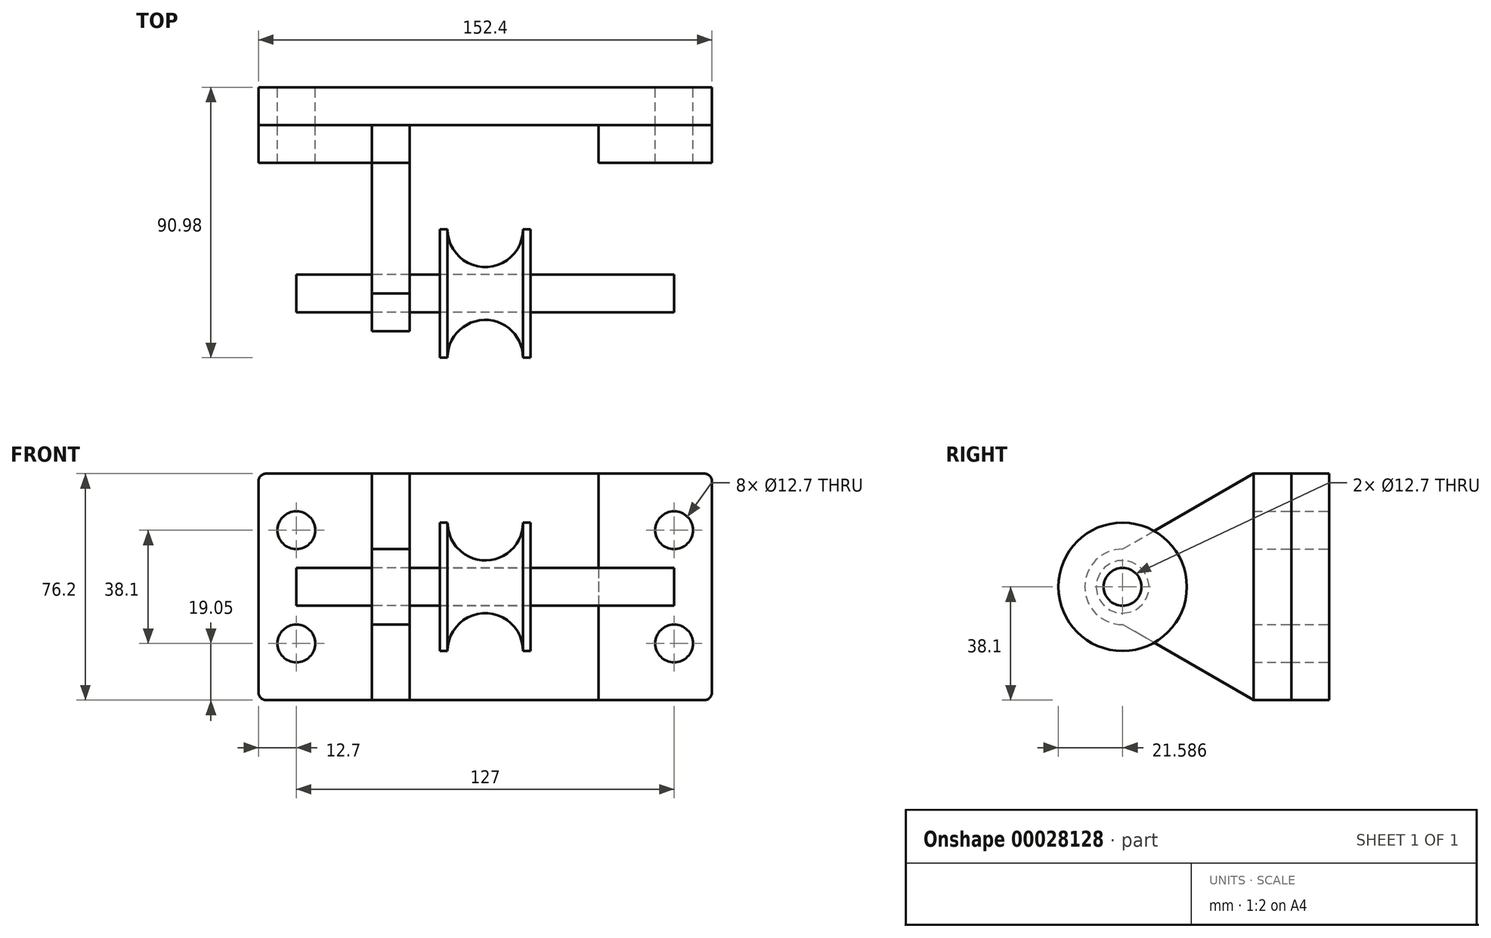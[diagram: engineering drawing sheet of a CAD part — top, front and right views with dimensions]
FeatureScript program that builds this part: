
annotation { "Feature Type Name" : "Feature", "Feature Type Description" : "" }
export const myFeature = defineFeature(function(context is Context, id is Id, definition is map)
    precondition{}
    {
        {
            var Q0;
            Q0=qCreatedBy(makeId("Front.planeOp"),FACE);
            var sketch = newSketch(context, id + "F0", { "sketchPlane" : qUnion([Q0])});
            skLineSegment(sketch, "E0.bottom", {"start": v(-76.2, 38.1) * mm, "end": v(76.2, 38.1) * mm});
            skLineSegment(sketch, "E0.top", {"start": v(-76.2, -38.1) * mm, "end": v(76.2, -38.1) * mm});
            skLineSegment(sketch, "E0.left", {"start": v(-76.2, 38.1) * mm, "end": v(-76.2, -38.1) * mm});
            skLineSegment(sketch, "E0.right", {"start": v(76.2, 38.1) * mm, "end": v(76.2, -38.1) * mm});
            skLineSegment(sketch, "E1", {"start": v(0, 38.1) * mm, "end": v(0, -38.1) * mm, "construction": true});
            skLineSegment(sketch, "E2", {"start": v(-76.2, 0) * mm, "end": v(76.2, 0) * mm, "construction": true});
            skCircle(sketch, "E3", {"center": v(-63.5, 19.05) * mm, "radius": 6.35 * mm});
            skCircle(sketch, "E4.MirrorC", {"center": v(63.5, 19.05) * mm, "radius": 6.35 * mm});
            skCircle(sketch, "E5.MirrorC", {"center": v(-63.5, -19.05) * mm, "radius": 6.35 * mm});
            skCircle(sketch, "E6.MirrorC", {"center": v(63.5, -19.05) * mm, "radius": 6.35 * mm});
            skSolve(sketch);
        }
        {
            var Q0;
            Q0=makeQuery(id+"F0.imprint","IMPRINT",FACE,{"disambiguationData":[TD([[makeQuery(id+"F0.imprint","IMPRINT",EDGE,{"derivedFrom":sQuery(id+"F0.wireOp",EDGE,"E0.bottom")}),-1.0]])]});
            extrude(context, id + "F1", {"entities" : qUnion([Q0]), "depth" : 12.7 * mm});
        }
        {
            var Q0;
            Q0=makeQuery(id+"F1.opExtrude","SWEPT_EDGE",EDGE,{"disambiguationData":[OSD([sQuery(id+"F0.wireOp",EDGE,"E0.bottom"),sQuery(id+"F0.wireOp",EDGE,"E0.left")])]});
            var Q1;
            Q1=makeQuery(id+"F1.opExtrude","SWEPT_EDGE",EDGE,{"disambiguationData":[OSD([sQuery(id+"F0.wireOp",EDGE,"E0.top"),sQuery(id+"F0.wireOp",EDGE,"E0.left")])]});
            var Q2;
            Q2=makeQuery(id+"F1.opExtrude","SWEPT_EDGE",EDGE,{"disambiguationData":[OSD([sQuery(id+"F0.wireOp",EDGE,"E0.bottom"),sQuery(id+"F0.wireOp",EDGE,"E0.right")])]});
            var Q3;
            Q3=makeQuery(id+"F1.opExtrude","SWEPT_EDGE",EDGE,{"disambiguationData":[OSD([sQuery(id+"F0.wireOp",EDGE,"E0.top"),sQuery(id+"F0.wireOp",EDGE,"E0.right")])]});
            fillet(context, id + "F2", {"entities" : qUnion([Q0, Q1, Q2, Q3]), "radius" : 2.54 * mm, "tangentPropagation" : true, "allowEdgeOverflow" : false});
        }
        {
            var Q0;
            Q0=makeQuery(id+"F1.opExtrude","CAP_FACE",FACE,{"disambiguationData":[OSD([sQuery(id+"F0.wireOp",EDGE,"E0.bottom"),sQuery(id+"F0.wireOp",EDGE,"E0.top"),sQuery(id+"F0.wireOp",EDGE,"E0.left"),sQuery(id+"F0.wireOp",EDGE,"E0.right"),sQuery(id+"F0.wireOp",EDGE,"E3"),sQuery(id+"F0.wireOp",EDGE,"E4.MirrorC"),sQuery(id+"F0.wireOp",EDGE,"E5.MirrorC"),sQuery(id+"F0.wireOp",EDGE,"E6.MirrorC")])],"isStart":false});
            var sketch = newSketch(context, id + "F3", { "sketchPlane" : qUnion([Q0])});
            skLineSegment(sketch, "E7.bottom", {"start": v(-76.2, 38.1) * mm, "end": v(-38.1, 38.1) * mm});
            skLineSegment(sketch, "E7.top", {"start": v(-76.2, -38.1) * mm, "end": v(-38.1, -38.1) * mm});
            skLineSegment(sketch, "E7.left", {"start": v(-76.2, 38.1) * mm, "end": v(-76.2, -38.1) * mm});
            skLineSegment(sketch, "E7.right", {"start": v(-38.1, 38.1) * mm, "end": v(-38.1, -38.1) * mm});
            skSolve(sketch);
        }
        {
            var Q0;
            {var subQ8=sQuery(id+"F3.wireOp",EDGE,"E7.right");Q0=makeQuery(id+"F3.imprint","IMPRINT",FACE,{"disambiguationData":[TD([[makeQuery(id+"F3.imprint","IMPRINT",EDGE,{"derivedFrom":subQ8}),-1.0]])]});}
            extrude(context, id + "F4", {"entities" : qUnion([Q0]), "depth" : 12.7 * mm});
        }
        {
            var Q0;
            Q0=makeQuery(id+"F4.opExtrude","SWEPT_FACE",FACE,{"disambiguationData":[OSD([sQuery(id+"F3.wireOp",EDGE,"E7.right")])]});
            cPlane(context, id + "F5", {"entities" : qUnion([Q0]), "cplaneType" : CPlaneType.OFFSET, "offset" : 0 * mm, "width" : 152.4 * mm, "height" : 152.4 * mm});
        }
        {
            var Q0;
            Q0=qCreatedBy(id+"F5.planeOp",FACE);
            var sketch = newSketch(context, id + "F6", { "sketchPlane" : qUnion([Q0])});
            skLineSegment(sketch, "E8.0", {"start": v(-25.4, -38.1) * mm, "end": v(-12.7, -38.1) * mm});
            skLineSegment(sketch, "E9.0", {"start": v(-25.4, 38.1) * mm, "end": v(-12.7, 38.1) * mm});
            skLineSegment(sketch, "E10.0", {"start": v(-25.4, 38.1) * mm, "end": v(-25.4, -38.1) * mm});
            skLineSegment(sketch, "E11", {"start": v(-12.7, -38.1) * mm, "end": v(-12.7, 38.1) * mm});
            skLineSegment(sketch, "E12", {"start": v(-25.4, -38.1) * mm, "end": v(-69.4, -12.7) * mm});
            skLineSegment(sketch, "E13", {"start": v(-69.4, -12.7) * mm, "end": v(-69.4, 12.7) * mm});
            skLineSegment(sketch, "E14", {"start": v(-69.4, 12.7) * mm, "end": v(-25.4, 38.1) * mm});
            skCircle(sketch, "E15", {"center": v(-69.4, 0) * mm, "radius": 6.35 * mm});
            skCircle(sketch, "E16", {"center": v(-69.4, 0) * mm, "radius": 12.7 * mm});
            skSolve(sketch);
        }
        {
            var Q0;
            Q0=makeQuery(id+"F6.imprint","IMPRINT",FACE,{"disambiguationData":[TD([[makeQuery(id+"F6.imprint","IMPRINT",EDGE,{"derivedFrom":sQuery(id+"F6.wireOp",EDGE,"E8.0")}),1.0]])]});
            var Q1;
            Q1=makeQuery(id+"F6.imprint","IMPRINT",FACE,{"disambiguationData":[TD([[makeQuery(id+"F6.imprint","IMPRINT",EDGE,{"derivedFrom":sQuery(id+"F6.wireOp",EDGE,"E10.0")}),-1.0]])]});
            var Q2;
            {var subQ1=sQuery(id+"F6.wireOp",EDGE,"E13");var subQ4=sQuery(id+"F6.wireOp",EDGE,"E15");var subQ6=makeQuery(id+"F6.imprint","INTERSECT",VERTEX,{"disambiguationData":[OD(0.0)],"derivedFrom":[subQ1,subQ4]});Q2=makeQuery(id+"F6.imprint","IMPRINT",FACE,{"disambiguationData":[TD([[makeQuery(id+"F6.imprint","IMPRINT",EDGE,{"disambiguationData":[TD([[subQ6,1.0]])],"derivedFrom":subQ4}),-1.0]])]});}
            var Q3;
            {var subQ1=sQuery(id+"F6.wireOp",EDGE,"E13");var subQ4=sQuery(id+"F6.wireOp",EDGE,"E15");var subQ6=makeQuery(id+"F6.imprint","INTERSECT",VERTEX,{"disambiguationData":[OD(0.0)],"derivedFrom":[subQ1,subQ4]});Q3=makeQuery(id+"F6.imprint","IMPRINT",FACE,{"disambiguationData":[TD([[makeQuery(id+"F6.imprint","IMPRINT",EDGE,{"disambiguationData":[TD([[subQ6,-1.0]])],"derivedFrom":subQ4}),-1.0]])]});}
            extrude(context, id + "F7", {"entities" : qUnion([Q0, Q1, Q2, Q3]), "depth" : 12.7 * mm});
        }
        {
            var Q0;
            Q0=makeQuery(id+"F4.opExtrude","SWEPT_BODY",BODY,{"disambiguationData":[OSD([sQuery(id+"F0.wireOp",EDGE,"E0.bottom"),sQuery(id+"F0.wireOp",EDGE,"E0.top"),sQuery(id+"F0.wireOp",EDGE,"E0.left"),sQuery(id+"F0.wireOp",EDGE,"E0.right"),sQuery(id+"F0.wireOp",EDGE,"E3"),sQuery(id+"F0.wireOp",EDGE,"E4.MirrorC"),sQuery(id+"F0.wireOp",EDGE,"E5.MirrorC"),sQuery(id+"F0.wireOp",EDGE,"E6.MirrorC"),sQuery(id+"F3.wireOp",EDGE,"E7.bottom"),sQuery(id+"F3.wireOp",EDGE,"E7.top"),sQuery(id+"F3.wireOp",EDGE,"E7.left"),sQuery(id+"F3.wireOp",EDGE,"E7.right")])]});
            var Q1;
            Q1=qCreatedBy(makeId("Right.planeOp"),FACE);
            mirror(context, id + "F8", {"entities" : qUnion([Q0]), "mirrorPlane" : qUnion([Q1])});
        }
        {
            var Q0;
            Q0=makeQuery(id+"F7.opExtrude","CAP_FACE",FACE,{"disambiguationData":[OSD([sQuery(id+"F6.wireOp",EDGE,"E8.0"),sQuery(id+"F6.wireOp",EDGE,"E9.0"),sQuery(id+"F6.wireOp",EDGE,"E11"),sQuery(id+"F6.wireOp",EDGE,"E12"),sQuery(id+"F6.wireOp",EDGE,"E14"),sQuery(id+"F6.wireOp",EDGE,"E15"),sQuery(id+"F6.wireOp",EDGE,"E16")])],"isStart":true});
            cPlane(context, id + "F9", {"entities" : qUnion([Q0]), "cplaneType" : CPlaneType.OFFSET, "offset" : 25.4 * mm, "width" : 152.4 * mm, "height" : 152.4 * mm});
        }
        {
            var Q0;
            Q0=qCreatedBy(id+"F9.planeOp",FACE);
            var sketch = newSketch(context, id + "F10", { "sketchPlane" : qUnion([Q0])});
            skCircle(sketch, "E17.0", {"center": v(69.4, 0) * mm, "radius": 6.35 * mm});
            skSolve(sketch);
        }
        {
            var Q0;
            Q0=makeQuery(id+"F10.imprint","IMPRINT",FACE,{"disambiguationData":[TD([[makeQuery(id+"F10.imprint","IMPRINT",EDGE,{"derivedFrom":sQuery(id+"F10.wireOp",EDGE,"E17.0")}),1.0]])]});
            extrude(context, id + "F11", {"entities" : qUnion([Q0]), "oppositeDirection" : true, "depth" : 127 * mm});
        }
        {
            var Q0;
            Q0=qCreatedBy(makeId("Top.planeOp"),FACE);
            var sketch = newSketch(context, id + "F12", { "sketchPlane" : qUnion([Q0])});
            skLineSegment(sketch, "E18", {"start": v(63.5, -75.74) * mm, "end": v(-63.5, -75.74) * mm});
            skLineSegment(sketch, "E19", {"start": v(-63.5, -63.04) * mm, "end": v(63.5, -63.04) * mm});
            skLineSegment(sketch, "E20.0", {"start": v(63.5, -75.74) * mm, "end": v(63.5, -63.04) * mm});
            skLineSegment(sketch, "E21.0", {"start": v(-63.5, -75.74) * mm, "end": v(-63.5, -63.04) * mm});
            skLineSegment(sketch, "E22", {"start": v(63.5, -69.4) * mm, "end": v(-63.5, -69.4) * mm, "construction": true});
            skLineSegment(sketch, "E23", {"start": v(0, -75.74) * mm, "end": v(0, -63.04) * mm, "construction": true});
            skArc(sketch, "E24", {"start": v(12.7, -90.98) * mm, "mid": v(0, -78.28) * mm, "end": v(-12.7, -90.98) * mm});
            skLineSegment(sketch, "E25", {"start": v(12.7, -90.98) * mm, "end": v(15.24, -90.98) * mm});
            skLineSegment(sketch, "E26", {"start": v(15.24, -90.98) * mm, "end": v(15.24, -75.74) * mm});
            skLineSegment(sketch, "E27", {"start": v(15.24, -75.74) * mm, "end": v(-15.24, -75.74) * mm});
            skLineSegment(sketch, "E28", {"start": v(-15.24, -75.74) * mm, "end": v(-15.24, -90.98) * mm});
            skLineSegment(sketch, "E29", {"start": v(-15.24, -90.98) * mm, "end": v(-12.7, -90.98) * mm});
            skSolve(sketch);
        }
        {
            var Q0;
            Q0=makeQuery(id+"F12.imprint","IMPRINT",FACE,{"disambiguationData":[TD([[makeQuery(id+"F12.imprint","IMPRINT",EDGE,{"derivedFrom":sQuery(id+"F12.wireOp",EDGE,"E24")}),-1.0]])]});
            var Q1;
            Q1=sQuery(id+"F12.wireOp",EDGE,"E22");
            revolve(context, id + "F13", {"entities" : qUnion([Q0]), "axis" : qUnion([Q1]), "revolveType" : RevolveType.FULL});
        }
    });
